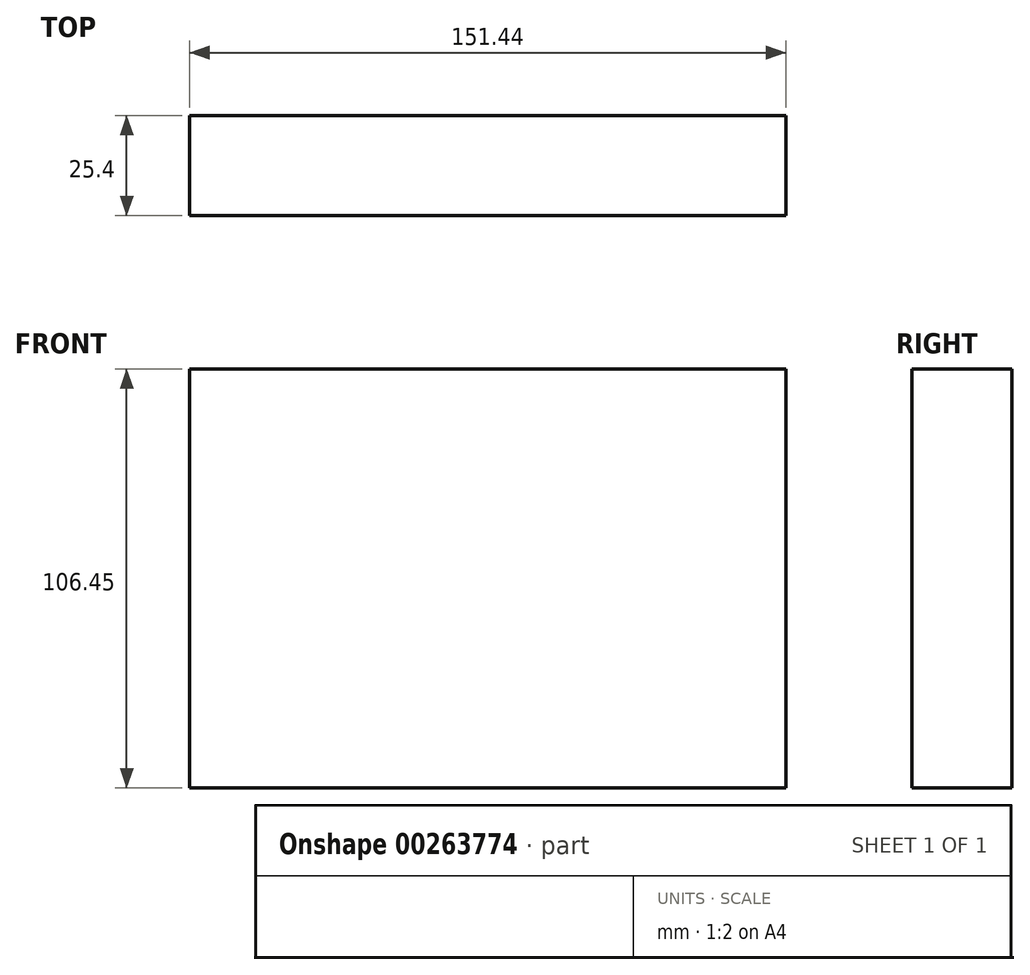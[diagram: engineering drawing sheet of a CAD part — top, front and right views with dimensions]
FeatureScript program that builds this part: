
annotation { "Feature Type Name" : "Feature", "Feature Type Description" : "" }
export const myFeature = defineFeature(function(context is Context, id is Id, definition is map)
    precondition{}
    {
        {
            var Q0;
            Q0=qCreatedBy(makeId("Front.planeOp"),FACE);
            var sketch = newSketch(context, id + "F0", { "sketchPlane" : qUnion([Q0])});
            skLineSegment(sketch, "E0.bottom", {"start": v(-72.22, 54.12) * mm, "end": v(79.22, 54.12) * mm});
            skLineSegment(sketch, "E0.top", {"start": v(-72.22, -52.33) * mm, "end": v(79.22, -52.33) * mm});
            skLineSegment(sketch, "E0.left", {"start": v(-72.22, 54.12) * mm, "end": v(-72.22, -52.33) * mm});
            skLineSegment(sketch, "E0.right", {"start": v(79.22, 54.12) * mm, "end": v(79.22, -52.33) * mm});
            skSolve(sketch);
        }
        {
            var Q0;
            Q0=makeQuery(id+"F0.imprint","IMPRINT",FACE,{"disambiguationData":[TD([[makeQuery(id+"F0.imprint","IMPRINT",EDGE,{"derivedFrom":sQuery(id+"F0.wireOp",EDGE,"E0.bottom")}),-1.0]])]});
            extrude(context, id + "F1", {"entities" : qUnion([Q0]), "depth" : 25.4 * mm});
        }
    });
